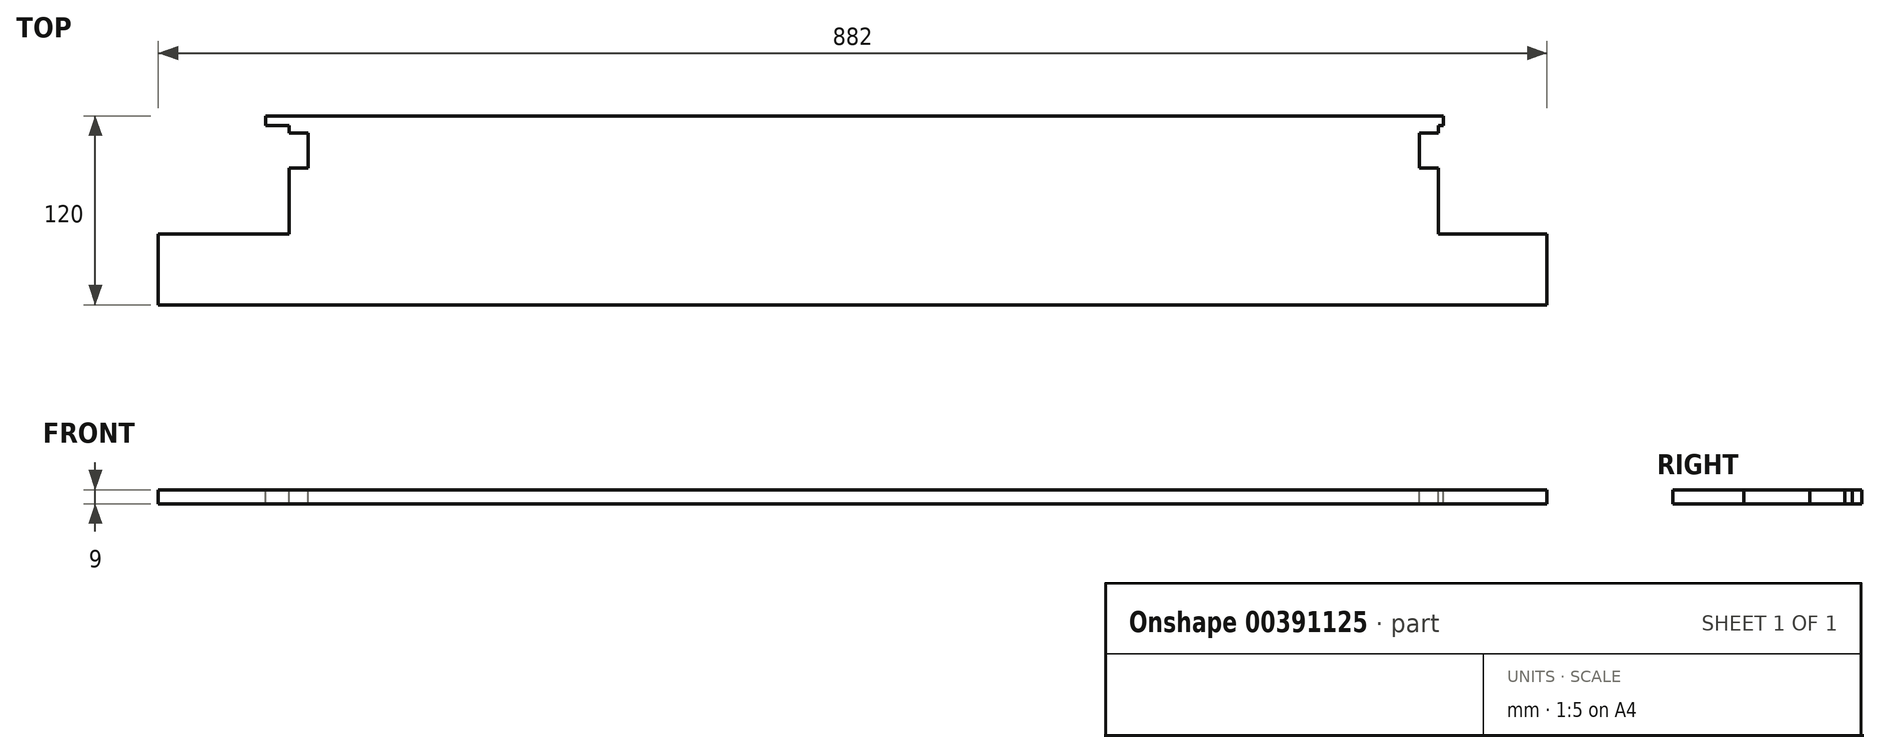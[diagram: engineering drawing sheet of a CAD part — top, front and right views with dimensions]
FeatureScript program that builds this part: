
annotation { "Feature Type Name" : "Feature", "Feature Type Description" : "" }
export const myFeature = defineFeature(function(context is Context, id is Id, definition is map)
    precondition{}
    {
        {
            var Q0;
            Q0=qCreatedBy(makeId("Top.planeOp"),FACE);
            var sketch = newSketch(context, id + "F0", { "sketchPlane" : qUnion([Q0])});
            skLineSegment(sketch, "E0.bottom", {"start": v(-45.92, 110.78) * mm, "end": v(836.08, 110.78) * mm});
            skLineSegment(sketch, "E0.top", {"start": v(-45.92, -9.22) * mm, "end": v(836.08, -9.22) * mm});
            skLineSegment(sketch, "E0.left", {"start": v(-45.92, 110.78) * mm, "end": v(-45.92, -9.22) * mm});
            skLineSegment(sketch, "E0.right", {"start": v(836.08, 110.78) * mm, "end": v(836.08, -9.22) * mm});
            skSolve(sketch);
        }
        {
            var Q0;
            Q0 = qSketchRegion(id + "F0", true);
            extrude(context, id + "F1", {"entities" : qUnion([Q0]), "depth" : 9 * mm});
        }
        {
            var Q0;
            Q0=makeQuery(id+"F1.opExtrude","CAP_FACE",FACE,{"disambiguationData":[OSD([sQuery(id+"F0.wireOp",EDGE,"E0.bottom"),sQuery(id+"F0.wireOp",EDGE,"E0.top"),sQuery(id+"F0.wireOp",EDGE,"E0.left"),sQuery(id+"F0.wireOp",EDGE,"E0.right")])],"isStart":false});
            var sketch = newSketch(context, id + "F2", { "sketchPlane" : qUnion([Q0])});
            skLineSegment(sketch, "E1", {"start": v(767.08, 104.78) * mm, "end": v(767.08, 99.78) * mm});
            skLineSegment(sketch, "E2", {"start": v(767.08, 99.78) * mm, "end": v(755.08, 99.78) * mm});
            skLineSegment(sketch, "E3", {"start": v(755.08, 99.78) * mm, "end": v(755.08, 77.78) * mm});
            skLineSegment(sketch, "E4", {"start": v(755.08, 77.78) * mm, "end": v(767.08, 77.78) * mm});
            skLineSegment(sketch, "E5", {"start": v(767.08, 77.78) * mm, "end": v(767.08, 35.78) * mm});
            skLineSegment(sketch, "E6", {"start": v(37.08, 35.78) * mm, "end": v(37.08, 77.78) * mm});
            skLineSegment(sketch, "E7", {"start": v(37.08, 77.78) * mm, "end": v(49.08, 77.78) * mm});
            skLineSegment(sketch, "E8", {"start": v(49.08, 77.78) * mm, "end": v(49.08, 99.78) * mm});
            skLineSegment(sketch, "E9", {"start": v(49.08, 99.78) * mm, "end": v(37.08, 99.78) * mm});
            skLineSegment(sketch, "E10", {"start": v(37.08, 99.78) * mm, "end": v(37.08, 104.78) * mm});
            skLineSegment(sketch, "E11", {"start": v(37.08, 35.78) * mm, "end": v(-45.92, 35.78) * mm});
            skLineSegment(sketch, "E12", {"start": v(767.08, 35.78) * mm, "end": v(836.08, 35.78) * mm});
            skLineSegment(sketch, "E13", {"start": v(37.08, 104.78) * mm, "end": v(22.08, 104.78) * mm});
            skLineSegment(sketch, "E14", {"start": v(22.08, 104.78) * mm, "end": v(22.08, 110.78) * mm});
            skLineSegment(sketch, "E15", {"start": v(770.08, 110.78) * mm, "end": v(770.08, 104.78) * mm});
            skLineSegment(sketch, "E16", {"start": v(770.08, 104.78) * mm, "end": v(767.08, 104.78) * mm});
            skLineSegment(sketch, "E17", {"start": v(22.08, 110.78) * mm, "end": v(-45.92, 110.78) * mm});
            skLineSegment(sketch, "E18", {"start": v(-45.92, 110.78) * mm, "end": v(-45.92, 35.78) * mm});
            skLineSegment(sketch, "E19", {"start": v(770.08, 110.78) * mm, "end": v(836.08, 110.78) * mm});
            skLineSegment(sketch, "E20", {"start": v(836.08, 110.78) * mm, "end": v(836.08, 35.78) * mm});
            skSolve(sketch);
        }
        {
            var Q0;
            Q0 = qSketchRegion(id + "F2", true);
            extrude(context, id + "F3", {"entities" : qUnion([Q0]), "operationType" : NewBodyOperationType.REMOVE, "endBound" : BoundingType.THROUGH_ALL, "oppositeDirection" : true, "depth" : 25 * mm});
        }
    });
